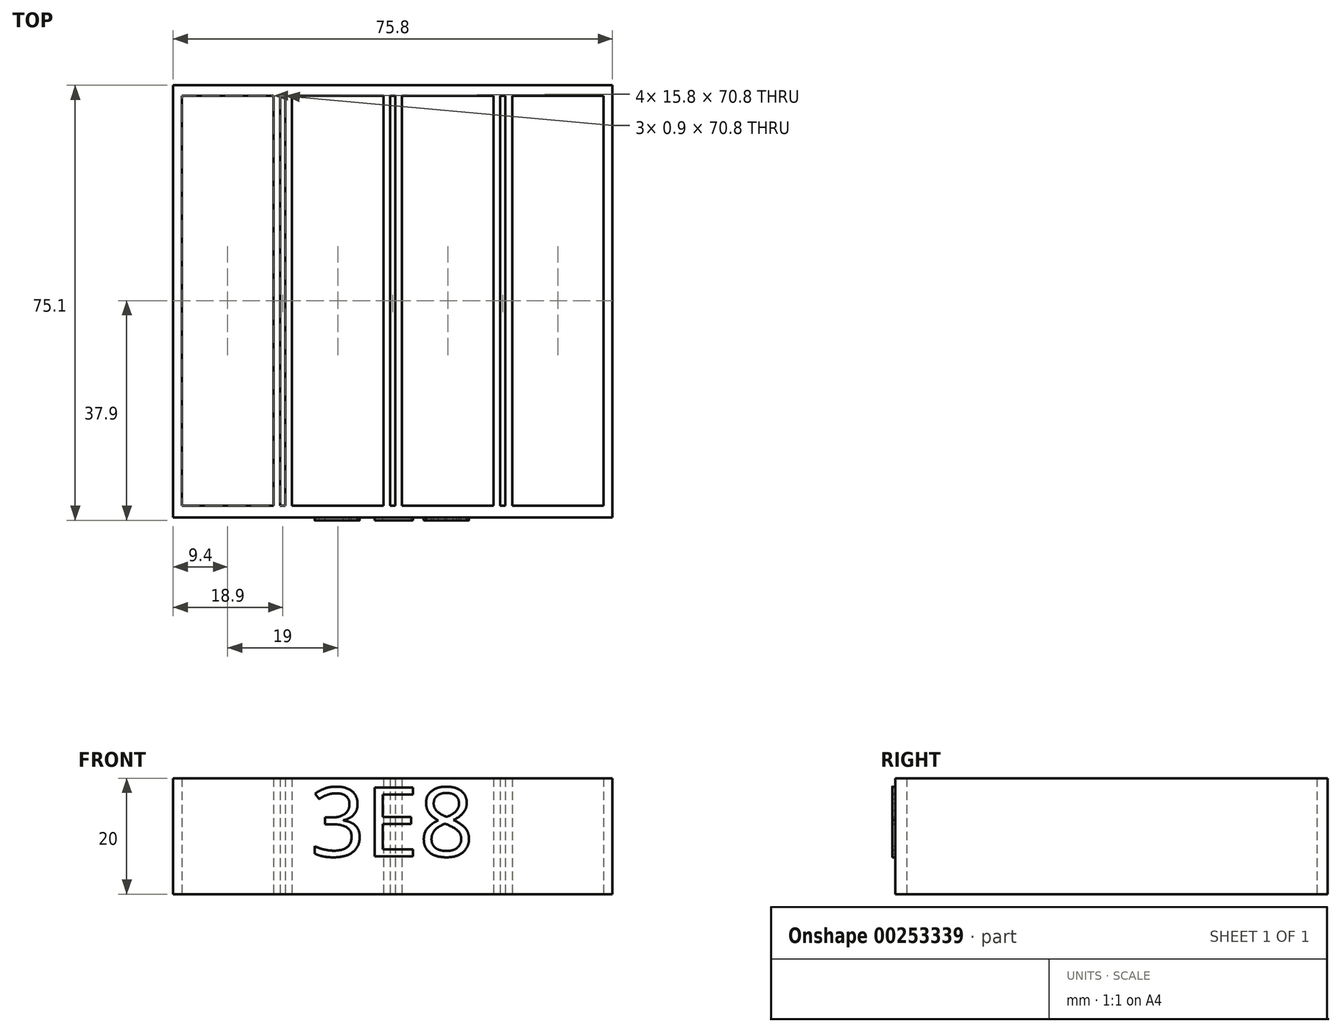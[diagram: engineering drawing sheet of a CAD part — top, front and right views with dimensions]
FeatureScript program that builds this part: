
annotation { "Feature Type Name" : "Feature", "Feature Type Description" : "" }
export const myFeature = defineFeature(function(context is Context, id is Id, definition is map)
    precondition{}
    {
        {
            var Q0;
            Q0=qCreatedBy(makeId("Top.planeOp"),FACE);
            var sketch = newSketch(context, id + "F0", { "sketchPlane" : qUnion([Q0])});
            skLineSegment(sketch, "E0.bottom", {"start": v(7.9, -35.4) * mm, "end": v(-7.9, -35.4) * mm});
            skLineSegment(sketch, "E0.top", {"start": v(7.9, 35.4) * mm, "end": v(-7.9, 35.4) * mm});
            skLineSegment(sketch, "E0.left", {"start": v(7.9, -35.4) * mm, "end": v(7.9, 35.4) * mm});
            skLineSegment(sketch, "E0.right", {"start": v(-7.9, -35.4) * mm, "end": v(-7.9, 35.4) * mm});
            skPoint(sketch, "E0.middle", {"position": v(0, 0) * mm});
            skLineSegment(sketch, "E1.0", {"start": v(-9.4, -37.4) * mm, "end": v(-9.4, 37.2) * mm});
            skPoint(sketch, "E2.1.0.0", {"position": v(19, 0) * mm});
            skLineSegment(sketch, "E2.1.0.1", {"start": v(11.1, -35.4) * mm, "end": v(11.1, 35.4) * mm});
            skLineSegment(sketch, "E2.1.0.2", {"start": v(26.9, 35.4) * mm, "end": v(11.1, 35.4) * mm});
            skLineSegment(sketch, "E2.1.0.3", {"start": v(26.9, -35.4) * mm, "end": v(26.9, 35.4) * mm});
            skLineSegment(sketch, "E2.1.0.4", {"start": v(26.9, -35.4) * mm, "end": v(11.1, -35.4) * mm});
            skPoint(sketch, "E2.2.0.0", {"position": v(38, 0) * mm});
            skLineSegment(sketch, "E2.2.0.1", {"start": v(30.1, -35.4) * mm, "end": v(30.1, 35.4) * mm});
            skLineSegment(sketch, "E2.2.0.2", {"start": v(45.9, 35.4) * mm, "end": v(30.1, 35.4) * mm});
            skLineSegment(sketch, "E2.2.0.3", {"start": v(45.9, -35.4) * mm, "end": v(45.9, 35.4) * mm});
            skLineSegment(sketch, "E2.2.0.4", {"start": v(45.9, -35.4) * mm, "end": v(30.1, -35.4) * mm});
            skPoint(sketch, "E2.3.0.0", {"position": v(57, 0) * mm});
            skLineSegment(sketch, "E2.3.0.1", {"start": v(49.1, -35.4) * mm, "end": v(49.1, 35.4) * mm});
            skLineSegment(sketch, "E2.3.0.2", {"start": v(64.9, 35.4) * mm, "end": v(49.1, 35.4) * mm});
            skLineSegment(sketch, "E2.3.0.3", {"start": v(64.9, -35.4) * mm, "end": v(64.9, 35.4) * mm});
            skLineSegment(sketch, "E2.3.0.4", {"start": v(64.9, -35.4) * mm, "end": v(49.1, -35.4) * mm});
            skLineSegment(sketch, "E2.3.0.7", {"start": v(66.4, -37.4) * mm, "end": v(66.4, 37.2) * mm});
            skLineSegment(sketch, "E2.direction1", {"start": v(0, 0) * mm, "end": v(19, 0) * mm, "construction": true});
            skLineSegment(sketch, "E3", {"start": v(-9.4, -37.4) * mm, "end": v(66.4, -37.4) * mm});
            skLineSegment(sketch, "E4", {"start": v(66.4, 37.2) * mm, "end": v(-9.4, 37.2) * mm});
            skLineSegment(sketch, "E5.bottom", {"start": v(9.05, 35.4) * mm, "end": v(9.95, 35.4) * mm});
            skLineSegment(sketch, "E5.top", {"start": v(9.05, -35.4) * mm, "end": v(9.95, -35.4) * mm});
            skLineSegment(sketch, "E5.left", {"start": v(9.05, 35.4) * mm, "end": v(9.05, -35.4) * mm});
            skLineSegment(sketch, "E5.right", {"start": v(9.95, 35.4) * mm, "end": v(9.95, -35.4) * mm});
            skPoint(sketch, "E5.middle", {"position": v(9.5, 0) * mm});
            skPoint(sketch, "E6.1.0.0", {"position": v(28.5, 0) * mm});
            skLineSegment(sketch, "E6.1.0.1", {"start": v(28.05, 35.4) * mm, "end": v(28.05, -35.4) * mm});
            skLineSegment(sketch, "E6.1.0.2", {"start": v(28.95, 35.4) * mm, "end": v(28.95, -35.4) * mm});
            skLineSegment(sketch, "E6.1.0.3", {"start": v(28.05, 35.4) * mm, "end": v(28.95, 35.4) * mm});
            skLineSegment(sketch, "E6.1.0.4", {"start": v(28.05, -35.4) * mm, "end": v(28.95, -35.4) * mm});
            skPoint(sketch, "E6.2.0.0", {"position": v(47.5, 0) * mm});
            skLineSegment(sketch, "E6.2.0.1", {"start": v(47.05, 35.4) * mm, "end": v(47.05, -35.4) * mm});
            skLineSegment(sketch, "E6.2.0.2", {"start": v(47.95, 35.4) * mm, "end": v(47.95, -35.4) * mm});
            skLineSegment(sketch, "E6.2.0.3", {"start": v(47.05, 35.4) * mm, "end": v(47.95, 35.4) * mm});
            skLineSegment(sketch, "E6.2.0.4", {"start": v(47.05, -35.4) * mm, "end": v(47.95, -35.4) * mm});
            skLineSegment(sketch, "E6.direction1", {"start": v(9.5, 0) * mm, "end": v(28.5, 0) * mm, "construction": true});
            skLineSegment(sketch, "E7", {"start": v(64.9, 0) * mm, "end": v(66.4, 0) * mm, "construction": true});
            skSolve(sketch);
        }
        {
            var Q0;
            Q0 = qSketchRegion(id + "F0", true);
            extrude(context, id + "F1", {"entities" : qUnion([Q0]), "depth" : 20 * mm});
        }
        {
            var Q0;
            Q0=makeQuery(id+"F1.opExtrude","SWEPT_FACE",FACE,{"disambiguationData":[OSD([sQuery(id+"F0.wireOp",EDGE,"E3")])]});
            var sketch = newSketch(context, id + "F2", { "sketchPlane" : qUnion([Q0])});
            skText(sketch, "E8", { "text": "3E8", "fontName": "OpenSans-Regular.ttf"});
            skLineSegment(sketch, "E9", {"start": v(-9.4, 0) * mm, "end": v(66.4, 20) * mm, "construction": true});
            skPoint(sketch, "E10", {"position": v(28.5, 10) * mm});
            const initialGuessF2  = {"E8": [0.01426, 0.00651, 1, 0, 0.01197]};
            skSetInitialGuess(sketch, initialGuessF2);
            skSolve(sketch);
        }
        {
            var Q0;
            Q0 = qSketchRegion(id + "F2", true);
            extrude(context, id + "F3", {"entities" : qUnion([Q0]), "operationType" : NewBodyOperationType.ADD, "depth" : .5 * mm});
        }
    });
